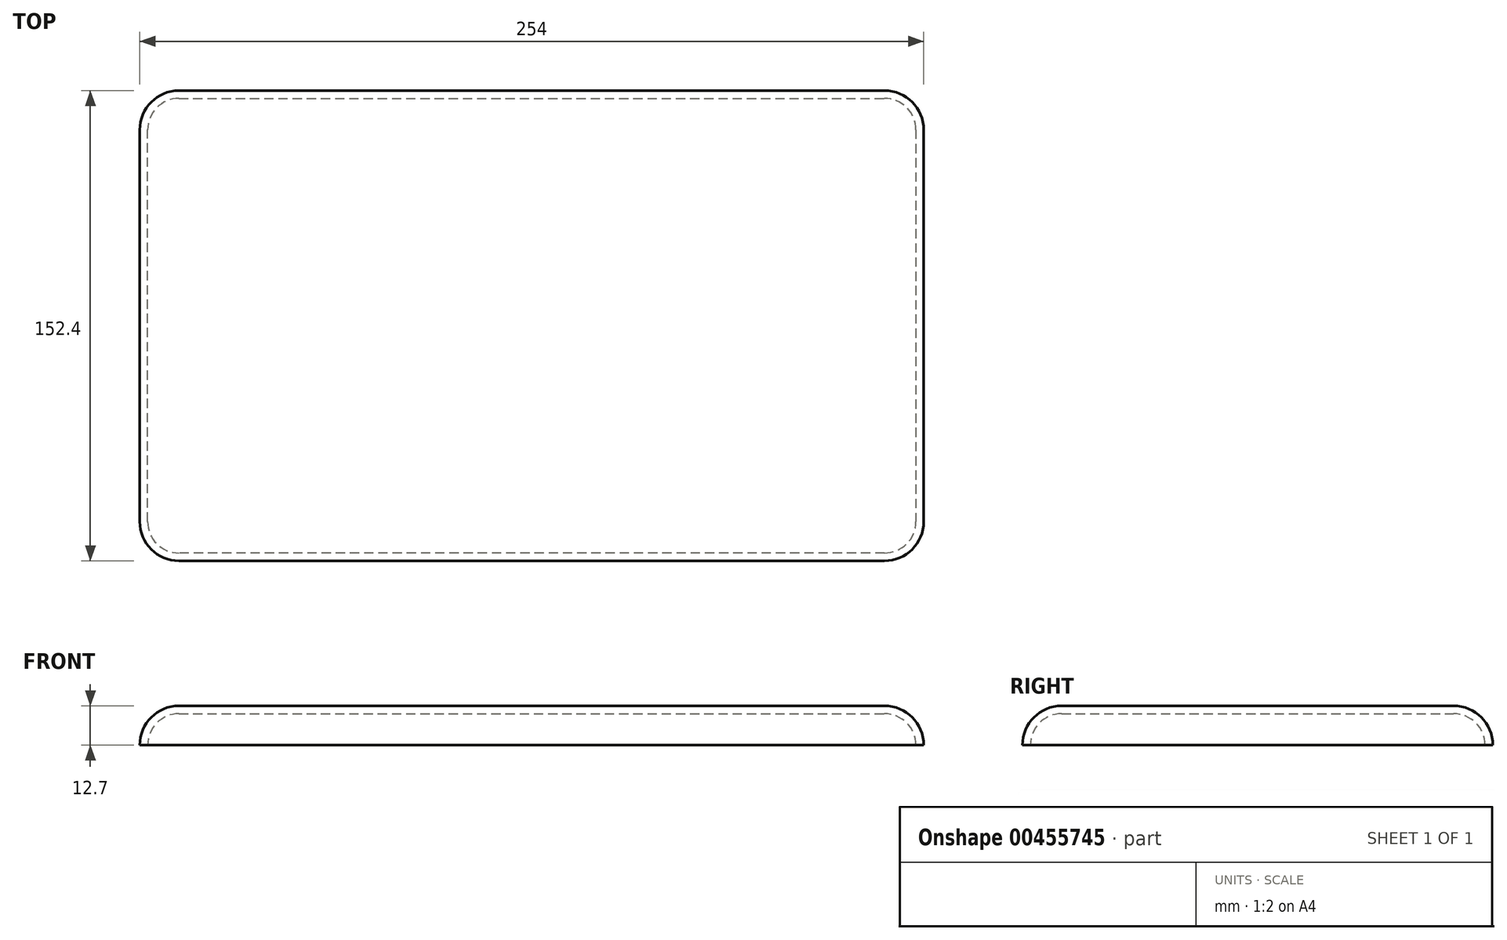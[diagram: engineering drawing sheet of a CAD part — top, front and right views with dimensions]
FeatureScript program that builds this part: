
annotation { "Feature Type Name" : "Feature", "Feature Type Description" : "" }
export const myFeature = defineFeature(function(context is Context, id is Id, definition is map)
    precondition{}
    {
        {
            var Q0;
            Q0=qCreatedBy(makeId("Top.planeOp"),FACE);
            var sketch = newSketch(context, id + "F0", { "sketchPlane" : qUnion([Q0])});
            skLineSegment(sketch, "E0.bottom", {"start": v(114.3, 76.2) * mm, "end": v(-114.3, 76.2) * mm});
            skLineSegment(sketch, "E0.top", {"start": v(114.3, -76.2) * mm, "end": v(-114.3, -76.2) * mm});
            skLineSegment(sketch, "E0.left", {"start": v(127, 63.5) * mm, "end": v(127, -63.5) * mm});
            skLineSegment(sketch, "E0.right", {"start": v(-127, 63.5) * mm, "end": v(-127, -63.5) * mm});
            skPoint(sketch, "E0.middle", {"position": v(0, 0) * mm});
            skPoint(sketch, "E1.visualSharp", {"position": v(-127, 76.2) * mm});
            skArc(sketch, "E1.filletArc", {"start": v(-114.3, 76.2) * mm, "mid": v(-123.28, 72.48) * mm, "end": v(-127, 63.5) * mm});
            skPoint(sketch, "E2.visualSharp", {"position": v(127, 76.2) * mm});
            skArc(sketch, "E2.filletArc", {"start": v(127, 63.5) * mm, "mid": v(123.28, 72.48) * mm, "end": v(114.3, 76.2) * mm});
            skPoint(sketch, "E3.visualSharp", {"position": v(127, -76.2) * mm});
            skArc(sketch, "E3.filletArc", {"start": v(114.3, -76.2) * mm, "mid": v(123.28, -72.48) * mm, "end": v(127, -63.5) * mm});
            skPoint(sketch, "E4.visualSharp", {"position": v(-127, -76.2) * mm});
            skArc(sketch, "E4.filletArc", {"start": v(-127, -63.5) * mm, "mid": v(-123.28, -72.48) * mm, "end": v(-114.3, -76.2) * mm});
            skSolve(sketch);
        }
        {
            var Q0;
            Q0 = qSketchRegion(id + "F0", true);
            extrude(context, id + "F1", {"entities" : qUnion([Q0]), "depth" : 12.7 * mm});
        }
        {
            var Q0;
            Q0=makeQuery(id+"F1.opExtrude","CAP_EDGE",EDGE,{"disambiguationData":[OSD([sQuery(id+"F0.wireOp",EDGE,"E0.top")])],"isStart":false});
            fillet(context, id + "F2", {"entities" : qUnion([Q0]), "radius" : 12.7 * mm, "tangentPropagation" : true, "allowEdgeOverflow" : false});
        }
        {
            var Q0;
            Q0=makeQuery(id+"F1.opExtrude","CAP_FACE",FACE,{"disambiguationData":[OSD([sQuery(id+"F0.wireOp",EDGE,"E0.bottom"),sQuery(id+"F0.wireOp",EDGE,"E0.top"),sQuery(id+"F0.wireOp",EDGE,"E0.left"),sQuery(id+"F0.wireOp",EDGE,"E0.right"),sQuery(id+"F0.wireOp",EDGE,"E1.filletArc"),sQuery(id+"F0.wireOp",EDGE,"E2.filletArc"),sQuery(id+"F0.wireOp",EDGE,"E3.filletArc"),sQuery(id+"F0.wireOp",EDGE,"E4.filletArc")])],"isStart":true});
            shell(context, id + "F3", {"entities" : qUnion([Q0]), "thickness" : 2.54 * mm});
        }
    });
